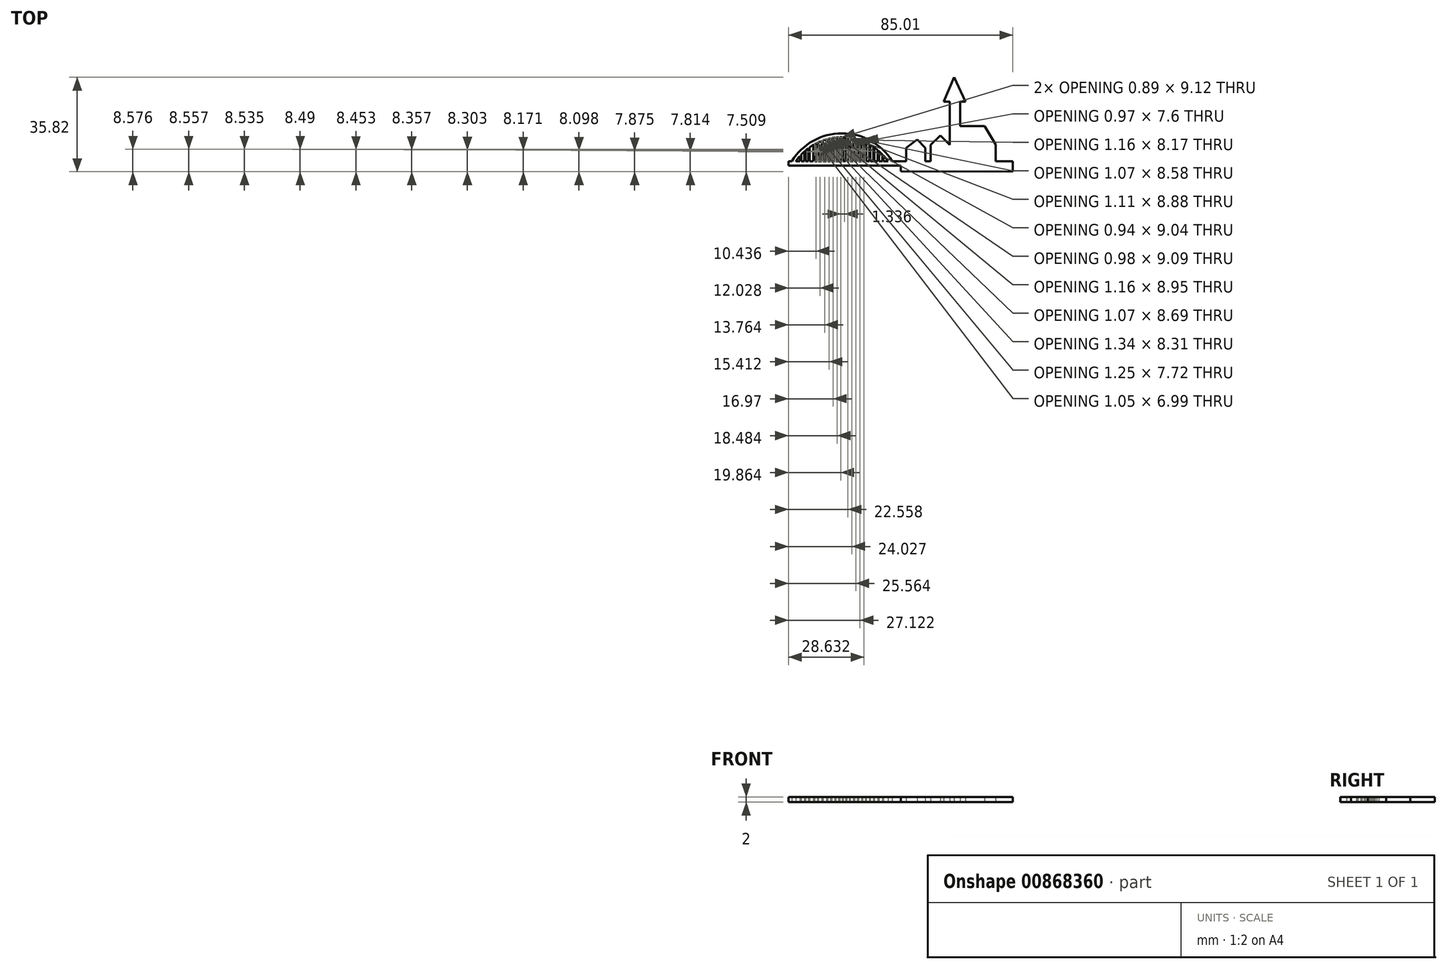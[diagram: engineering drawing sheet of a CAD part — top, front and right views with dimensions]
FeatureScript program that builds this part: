
annotation { "Feature Type Name" : "Feature", "Feature Type Description" : "" }
export const myFeature = defineFeature(function(context is Context, id is Id, definition is map)
    precondition{}
    {
        {
            var Q0;
            Q0=qCreatedBy(makeId("Top.planeOp"),FACE);
            var sketch = newSketch(context, id + "F0", { "sketchPlane" : qUnion([Q0])});
            skLineSegment(sketch, "E0.bottom", {"start": v(42.5, -30) * mm, "end": v(-42.5, -30) * mm});
            skLineSegment(sketch, "E0.top", {"start": v(42.5, 30) * mm, "end": v(-42.5, 30) * mm});
            skLineSegment(sketch, "E0.left", {"start": v(42.5, -30) * mm, "end": v(42.5, 30) * mm});
            skLineSegment(sketch, "E0.right", {"start": v(-42.5, -30) * mm, "end": v(-42.5, 30) * mm});
            skPoint(sketch, "E0.middle", {"position": v(0, 0) * mm});
            skSolve(sketch);
        }
        {
            var Q0;
            Q0=makeQuery(id+"F0.imprint","IMPRINT",FACE,{"disambiguationData":[TD([[makeQuery(id+"F0.imprint","IMPRINT",EDGE,{"derivedFrom":sQuery(id+"F0.wireOp",EDGE,"E0.bottom")}),-1.0]])]});
            var sketch = newSketch(context, id + "F1", { "sketchPlane" : qUnion([Q0])});
            skLineSegment(sketch, "E1.bottom", {"start": v(-42.57, -27.66) * mm, "end": v(0, -27.66) * mm});
            skLineSegment(sketch, "E1.top", {"start": v(-42.57, -25.97) * mm, "end": v(0, -25.97) * mm});
            skLineSegment(sketch, "E1.left", {"start": v(-42.57, -27.66) * mm, "end": v(-42.57, -25.97) * mm});
            skLineSegment(sketch, "E1.right", {"start": v(0, -27.66) * mm, "end": v(0, -25.97) * mm});
            skArc(sketch, "E2", {"start": v(-3.25, -25.97) * mm, "mid": v(-22.26, -15.39) * mm, "end": v(-41.27, -25.97) * mm});
            skArc(sketch, "E3", {"start": v(-4.87, -25.97) * mm, "mid": v(-22.33, -16.84) * mm, "end": v(-39.8, -25.97) * mm});
            skLineSegment(sketch, "E4", {"start": v(-33.34, -25.97) * mm, "end": v(-33.34, -19.92) * mm});
            skLineSegment(sketch, "E5", {"start": v(-33.34, -19.92) * mm, "end": v(-34.15, -20.43) * mm});
            skLineSegment(sketch, "E6", {"start": v(-34.15, -20.43) * mm, "end": v(-34.15, -25.97) * mm});
            skLineSegment(sketch, "E7", {"start": v(-34.15, -25.97) * mm, "end": v(-33.34, -25.97) * mm});
            skLineSegment(sketch, "E8", {"start": v(-36.62, -25.97) * mm, "end": v(-36.62, -22.36) * mm});
            skLineSegment(sketch, "E9", {"start": v(-36.62, -22.36) * mm, "end": v(-37.42, -23.12) * mm});
            skLineSegment(sketch, "E10", {"start": v(-37.42, -23.12) * mm, "end": v(-37.42, -25.97) * mm});
            skLineSegment(sketch, "E11", {"start": v(-37.42, -25.97) * mm, "end": v(-36.62, -25.97) * mm});
            skLineSegment(sketch, "E12", {"start": v(-30.9, -25.97) * mm, "end": v(-30.9, -18.65) * mm});
            skLineSegment(sketch, "E13", {"start": v(-30.9, -18.65) * mm, "end": v(-29.78, -18.2) * mm});
            skLineSegment(sketch, "E14", {"start": v(-29.78, -18.2) * mm, "end": v(-29.78, -25.97) * mm});
            skLineSegment(sketch, "E15", {"start": v(-29.78, -25.97) * mm, "end": v(-30.9, -25.97) * mm});
            skLineSegment(sketch, "E16", {"start": v(-27.67, -17.53) * mm, "end": v(-27.67, -25.97) * mm});
            skLineSegment(sketch, "E17", {"start": v(-27.67, -25.97) * mm, "end": v(-26.67, -25.97) * mm});
            skLineSegment(sketch, "E18", {"start": v(-26.67, -25.97) * mm, "end": v(-26.67, -17.3) * mm});
            skLineSegment(sketch, "E19", {"start": v(-26.67, -17.3) * mm, "end": v(-27.67, -17.53) * mm});
            skLineSegment(sketch, "E20", {"start": v(-24.95, -17) * mm, "end": v(-24.95, -25.97) * mm});
            skLineSegment(sketch, "E21", {"start": v(-24.95, -25.97) * mm, "end": v(-24.13, -25.97) * mm});
            skLineSegment(sketch, "E22", {"start": v(-24.13, -25.97) * mm, "end": v(-24.13, -16.92) * mm});
            skLineSegment(sketch, "E23", {"start": v(-24.13, -16.92) * mm, "end": v(-24.95, -17) * mm});
            skLineSegment(sketch, "E24", {"start": v(-22.33, -16.84) * mm, "end": v(-22.33, -25.97) * mm});
            skLineSegment(sketch, "E25", {"start": v(-22.33, -25.97) * mm, "end": v(-21.28, -25.97) * mm});
            skLineSegment(sketch, "E26", {"start": v(-21.28, -25.97) * mm, "end": v(-21.28, -16.87) * mm});
            skLineSegment(sketch, "E27", {"start": v(-21.28, -16.87) * mm, "end": v(-22.33, -16.84) * mm});
            skLineSegment(sketch, "E28", {"start": v(-19.68, -25.97) * mm, "end": v(-19.68, -17) * mm});
            skLineSegment(sketch, "E29", {"start": v(-19.68, -17) * mm, "end": v(-18.66, -17.16) * mm});
            skLineSegment(sketch, "E30", {"start": v(-18.66, -17.16) * mm, "end": v(-18.66, -25.97) * mm});
            skLineSegment(sketch, "E31", {"start": v(-18.66, -25.97) * mm, "end": v(-19.68, -25.97) * mm});
            skLineSegment(sketch, "E32", {"start": v(-17.03, -25.97) * mm, "end": v(-17.03, -17.51) * mm});
            skLineSegment(sketch, "E33", {"start": v(-17.03, -17.51) * mm, "end": v(-16, -17.8) * mm});
            skLineSegment(sketch, "E34", {"start": v(-16, -17.8) * mm, "end": v(-16, -25.97) * mm});
            skLineSegment(sketch, "E35", {"start": v(-16, -25.97) * mm, "end": v(-17.03, -25.97) * mm});
            skLineSegment(sketch, "E36", {"start": v(-14.54, -25.97) * mm, "end": v(-14.54, -18.32) * mm});
            skLineSegment(sketch, "E37", {"start": v(-14.54, -18.32) * mm, "end": v(-13.53, -18.75) * mm});
            skLineSegment(sketch, "E38", {"start": v(-13.53, -18.75) * mm, "end": v(-13.53, -25.97) * mm});
            skLineSegment(sketch, "E39", {"start": v(-13.53, -25.97) * mm, "end": v(-14.54, -25.97) * mm});
            skLineSegment(sketch, "E40", {"start": v(-11.58, -25.97) * mm, "end": v(-11.58, -19.76) * mm});
            skLineSegment(sketch, "E41", {"start": v(-11.58, -19.76) * mm, "end": v(-10.75, -20.27) * mm});
            skLineSegment(sketch, "E42", {"start": v(-10.75, -20.27) * mm, "end": v(-10.75, -25.97) * mm});
            skLineSegment(sketch, "E43", {"start": v(-10.75, -25.97) * mm, "end": v(-11.58, -25.97) * mm});
            skLineSegment(sketch, "E44", {"start": v(-9.2, -25.97) * mm, "end": v(-9.2, -21.38) * mm});
            skLineSegment(sketch, "E45", {"start": v(-9.2, -21.38) * mm, "end": v(-8.03, -22.36) * mm});
            skLineSegment(sketch, "E46", {"start": v(-8.03, -22.36) * mm, "end": v(-8.61, -21.87) * mm});
            skLineSegment(sketch, "E47", {"start": v(-8.61, -21.87) * mm, "end": v(-8.61, -25.97) * mm});
            skLineSegment(sketch, "E48", {"start": v(-8.61, -25.97) * mm, "end": v(-9.2, -25.97) * mm});
            skLineSegment(sketch, "E49", {"start": v(-7.28, -25.97) * mm, "end": v(-7.28, -23.07) * mm});
            skLineSegment(sketch, "E50", {"start": v(-7.28, -23.07) * mm, "end": v(-6.8, -23.57) * mm});
            skLineSegment(sketch, "E51", {"start": v(-6.8, -23.57) * mm, "end": v(-6.8, -25.97) * mm});
            skLineSegment(sketch, "E52", {"start": v(-6.8, -25.97) * mm, "end": v(-7.28, -25.97) * mm});
            skLineSegment(sketch, "E53", {"start": v(0, -29.8) * mm, "end": v(0, -25.97) * mm});
            skLineSegment(sketch, "E54", {"start": v(2.02, -25.97) * mm, "end": v(2.02, -20.96) * mm});
            skLineSegment(sketch, "E55", {"start": v(2.02, -20.96) * mm, "end": v(6.25, -17.79) * mm});
            skLineSegment(sketch, "E56", {"start": v(6.25, -17.79) * mm, "end": v(9.32, -20.96) * mm});
            skLineSegment(sketch, "E57", {"start": v(9.32, -20.96) * mm, "end": v(9.32, -25.97) * mm});
            skLineSegment(sketch, "E58", {"start": v(9.32, -25.97) * mm, "end": v(11.3, -25.97) * mm});
            skLineSegment(sketch, "E59", {"start": v(11.3, -25.97) * mm, "end": v(11.3, -19.72) * mm});
            skLineSegment(sketch, "E60", {"start": v(11.3, -19.72) * mm, "end": v(15, -16.15) * mm});
            skLineSegment(sketch, "E61", {"start": v(15, -16.15) * mm, "end": v(18.53, -19.8) * mm});
            skLineSegment(sketch, "E62", {"start": v(18.53, -19.8) * mm, "end": v(18.53, -25.97) * mm});
            skLineSegment(sketch, "E63", {"start": v(18.53, -25.97) * mm, "end": v(18.53, -3.42) * mm});
            skLineSegment(sketch, "E64", {"start": v(18.53, -3.42) * mm, "end": v(16.26, -3.42) * mm});
            skLineSegment(sketch, "E65", {"start": v(16.26, -3.42) * mm, "end": v(20.2, 5.84) * mm});
            skLineSegment(sketch, "E66", {"start": v(20.2, 5.84) * mm, "end": v(24.53, -3.42) * mm});
            skLineSegment(sketch, "E67", {"start": v(24.53, -3.42) * mm, "end": v(22.49, -3.42) * mm});
            skLineSegment(sketch, "E68", {"start": v(22.49, -3.42) * mm, "end": v(22.49, -19.63) * mm});
            skLineSegment(sketch, "E69", {"start": v(22.49, -19.63) * mm, "end": v(22.49, -12.61) * mm});
            skLineSegment(sketch, "E70", {"start": v(22.49, -12.61) * mm, "end": v(31.8, -12.61) * mm});
            skLineSegment(sketch, "E71", {"start": v(31.8, -12.61) * mm, "end": v(35.96, -19.63) * mm});
            skLineSegment(sketch, "E72", {"start": v(35.96, -19.63) * mm, "end": v(35.96, -25.97) * mm});
            skLineSegment(sketch, "E73", {"start": v(35.96, -25.97) * mm, "end": v(37.84, -25.97) * mm});
            skLineSegment(sketch, "E74", {"start": v(37.84, -25.97) * mm, "end": v(42.44, -25.97) * mm});
            skLineSegment(sketch, "E75", {"start": v(42.44, -25.97) * mm, "end": v(42.44, -29.98) * mm});
            skLineSegment(sketch, "E76", {"start": v(42.44, -29.98) * mm, "end": v(0, -29.8) * mm});
            skLineSegment(sketch, "E77", {"start": v(0, -25.97) * mm, "end": v(2.02, -25.97) * mm});
            skSolve(sketch);
        }
        {
            var Q0;
            Q0 = qSketchRegion(id + "F1", true);
            extrude(context, id + "F2", {"entities" : qUnion([Q0]), "depth" : 2 * mm, "offsetDistance" : 25 * mm});
        }
        {
            var Q0;
            Q0=makeQuery(id+"F0.imprint","IMPRINT",FACE,{"disambiguationData":[TD([[makeQuery(id+"F0.imprint","IMPRINT",EDGE,{"derivedFrom":sQuery(id+"F0.wireOp",EDGE,"E0.bottom")}),-1.0]])]});
            var sketch = newSketch(context, id + "F3", { "sketchPlane" : qUnion([Q0])});
            skLineSegment(sketch, "E78.bottom", {"start": v(-38.16, -26.15) * mm, "end": v(-37.76, -26.15) * mm});
            skLineSegment(sketch, "E78.top", {"start": v(-38.16, -23.06) * mm, "end": v(-37.76, -23.06) * mm});
            skLineSegment(sketch, "E78.left", {"start": v(-38.16, -26.15) * mm, "end": v(-38.16, -23.06) * mm});
            skLineSegment(sketch, "E78.right", {"start": v(-37.76, -26.15) * mm, "end": v(-37.76, -23.06) * mm});
            skLineSegment(sketch, "E79.bottom", {"start": v(-36.55, -26.06) * mm, "end": v(-36.1, -26.06) * mm});
            skLineSegment(sketch, "E79.top", {"start": v(-36.55, -21.75) * mm, "end": v(-36.1, -21.75) * mm});
            skLineSegment(sketch, "E79.left", {"start": v(-36.55, -26.06) * mm, "end": v(-36.55, -21.75) * mm});
            skLineSegment(sketch, "E79.right", {"start": v(-36.1, -26.06) * mm, "end": v(-36.1, -21.75) * mm});
            skLineSegment(sketch, "E80.bottom", {"start": v(-35, -26.02) * mm, "end": v(-34.55, -26.02) * mm});
            skLineSegment(sketch, "E80.top", {"start": v(-35, -20.45) * mm, "end": v(-34.55, -20.45) * mm});
            skLineSegment(sketch, "E80.left", {"start": v(-35, -26.02) * mm, "end": v(-35, -20.45) * mm});
            skLineSegment(sketch, "E80.right", {"start": v(-34.55, -26.02) * mm, "end": v(-34.55, -20.45) * mm});
            skLineSegment(sketch, "E81.bottom", {"start": v(-33.1, -26.02) * mm, "end": v(-32.66, -26.02) * mm});
            skLineSegment(sketch, "E81.top", {"start": v(-33.1, -19.3) * mm, "end": v(-32.66, -19.3) * mm});
            skLineSegment(sketch, "E81.left", {"start": v(-33.1, -26.02) * mm, "end": v(-33.1, -19.3) * mm});
            skLineSegment(sketch, "E81.right", {"start": v(-32.66, -26.02) * mm, "end": v(-32.66, -19.3) * mm});
            skLineSegment(sketch, "E82.bottom", {"start": v(-31.61, -26.06) * mm, "end": v(-31.17, -26.06) * mm});
            skLineSegment(sketch, "E82.top", {"start": v(-31.61, -18.34) * mm, "end": v(-31.17, -18.34) * mm});
            skLineSegment(sketch, "E82.left", {"start": v(-31.61, -26.06) * mm, "end": v(-31.61, -18.34) * mm});
            skLineSegment(sketch, "E82.right", {"start": v(-31.17, -26.06) * mm, "end": v(-31.17, -18.34) * mm});
            skLineSegment(sketch, "E83.bottom", {"start": v(-29.92, -26.06) * mm, "end": v(-29.47, -26.06) * mm});
            skLineSegment(sketch, "E83.top", {"start": v(-29.92, -17.7) * mm, "end": v(-29.47, -17.7) * mm});
            skLineSegment(sketch, "E83.left", {"start": v(-29.92, -26.06) * mm, "end": v(-29.92, -17.7) * mm});
            skLineSegment(sketch, "E83.right", {"start": v(-29.47, -26.06) * mm, "end": v(-29.47, -17.7) * mm});
            skLineSegment(sketch, "E84.bottom", {"start": v(-28.14, -26.1) * mm, "end": v(-27.7, -26.1) * mm});
            skLineSegment(sketch, "E84.top", {"start": v(-28.14, -17.27) * mm, "end": v(-27.7, -17.27) * mm});
            skLineSegment(sketch, "E84.left", {"start": v(-28.14, -26.1) * mm, "end": v(-28.14, -17.27) * mm});
            skLineSegment(sketch, "E84.right", {"start": v(-27.7, -26.1) * mm, "end": v(-27.7, -17.27) * mm});
            skLineSegment(sketch, "E85.bottom", {"start": v(-26.62, -26.09) * mm, "end": v(-26.18, -26.09) * mm});
            skLineSegment(sketch, "E85.top", {"start": v(-26.62, -16.98) * mm, "end": v(-26.18, -16.98) * mm});
            skLineSegment(sketch, "E85.left", {"start": v(-26.62, -26.09) * mm, "end": v(-26.62, -16.98) * mm});
            skLineSegment(sketch, "E85.right", {"start": v(-26.18, -26.09) * mm, "end": v(-26.18, -16.98) * mm});
            skLineSegment(sketch, "E86.bottom", {"start": v(-25.02, -26.09) * mm, "end": v(-24.58, -26.09) * mm});
            skLineSegment(sketch, "E86.top", {"start": v(-25.02, -16.58) * mm, "end": v(-24.58, -16.58) * mm});
            skLineSegment(sketch, "E86.left", {"start": v(-25.02, -26.09) * mm, "end": v(-25.02, -16.58) * mm});
            skLineSegment(sketch, "E86.right", {"start": v(-24.58, -26.09) * mm, "end": v(-24.58, -16.58) * mm});
            skLineSegment(sketch, "E87.bottom", {"start": v(-23.6, -26.09) * mm, "end": v(-23.15, -26.09) * mm});
            skLineSegment(sketch, "E87.top", {"start": v(-23.6, -16.58) * mm, "end": v(-23.15, -16.58) * mm});
            skLineSegment(sketch, "E87.left", {"start": v(-23.6, -26.09) * mm, "end": v(-23.6, -16.58) * mm});
            skLineSegment(sketch, "E87.right", {"start": v(-23.15, -26.09) * mm, "end": v(-23.15, -16.58) * mm});
            skLineSegment(sketch, "E88.bottom", {"start": v(-22.26, -26.02) * mm, "end": v(-21.82, -26.02) * mm});
            skLineSegment(sketch, "E88.top", {"start": v(-22.26, -16.58) * mm, "end": v(-21.82, -16.58) * mm});
            skLineSegment(sketch, "E88.left", {"start": v(-22.26, -26.02) * mm, "end": v(-22.26, -16.58) * mm});
            skLineSegment(sketch, "E88.right", {"start": v(-21.82, -26.02) * mm, "end": v(-21.82, -16.58) * mm});
            skLineSegment(sketch, "E89.bottom", {"start": v(-20.92, -26.09) * mm, "end": v(-20.48, -26.09) * mm});
            skLineSegment(sketch, "E89.top", {"start": v(-20.92, -16.58) * mm, "end": v(-20.48, -16.58) * mm});
            skLineSegment(sketch, "E89.left", {"start": v(-20.92, -26.09) * mm, "end": v(-20.92, -16.58) * mm});
            skLineSegment(sketch, "E89.right", {"start": v(-20.48, -26.09) * mm, "end": v(-20.48, -16.58) * mm});
            skLineSegment(sketch, "E90.bottom", {"start": v(-19.54, -26.02) * mm, "end": v(-19.1, -26.02) * mm});
            skLineSegment(sketch, "E90.top", {"start": v(-19.54, -16.58) * mm, "end": v(-19.1, -16.58) * mm});
            skLineSegment(sketch, "E90.left", {"start": v(-19.54, -26.02) * mm, "end": v(-19.54, -16.58) * mm});
            skLineSegment(sketch, "E90.right", {"start": v(-19.1, -26.02) * mm, "end": v(-19.1, -16.58) * mm});
            skLineSegment(sketch, "E91.bottom", {"start": v(-17.99, -26.02) * mm, "end": v(-17.54, -26.02) * mm});
            skLineSegment(sketch, "E91.top", {"start": v(-17.99, -16.58) * mm, "end": v(-17.54, -16.58) * mm});
            skLineSegment(sketch, "E91.left", {"start": v(-17.99, -26.02) * mm, "end": v(-17.99, -16.58) * mm});
            skLineSegment(sketch, "E91.right", {"start": v(-17.54, -26.02) * mm, "end": v(-17.54, -16.58) * mm});
            skLineSegment(sketch, "E92.bottom", {"start": v(-16.03, -26.1) * mm, "end": v(-16.47, -26.1) * mm});
            skLineSegment(sketch, "E92.top", {"start": v(-16.03, -17.03) * mm, "end": v(-16.47, -17.03) * mm});
            skLineSegment(sketch, "E92.left", {"start": v(-16.03, -26.1) * mm, "end": v(-16.03, -17.03) * mm});
            skLineSegment(sketch, "E92.right", {"start": v(-16.47, -26.1) * mm, "end": v(-16.47, -17.03) * mm});
            skLineSegment(sketch, "E93.bottom", {"start": v(-14.87, -26.06) * mm, "end": v(-14.42, -26.06) * mm});
            skLineSegment(sketch, "E93.top", {"start": v(-14.87, -17.6) * mm, "end": v(-14.42, -17.6) * mm});
            skLineSegment(sketch, "E93.left", {"start": v(-14.87, -26.06) * mm, "end": v(-14.87, -17.6) * mm});
            skLineSegment(sketch, "E93.right", {"start": v(-14.42, -26.06) * mm, "end": v(-14.42, -17.6) * mm});
            skLineSegment(sketch, "E94.bottom", {"start": v(-13.45, -26.04) * mm, "end": v(-13, -26.04) * mm});
            skLineSegment(sketch, "E94.top", {"start": v(-13.45, -17.87) * mm, "end": v(-13, -17.87) * mm});
            skLineSegment(sketch, "E94.left", {"start": v(-13.45, -26.04) * mm, "end": v(-13.45, -17.87) * mm});
            skLineSegment(sketch, "E94.right", {"start": v(-13, -26.04) * mm, "end": v(-13, -17.87) * mm});
            skLineSegment(sketch, "E95.bottom", {"start": v(-11.95, -26.04) * mm, "end": v(-11.5, -26.04) * mm});
            skLineSegment(sketch, "E95.top", {"start": v(-11.95, -19.27) * mm, "end": v(-11.5, -19.27) * mm});
            skLineSegment(sketch, "E95.left", {"start": v(-11.95, -26.04) * mm, "end": v(-11.95, -19.27) * mm});
            skLineSegment(sketch, "E95.right", {"start": v(-11.5, -26.04) * mm, "end": v(-11.5, -19.27) * mm});
            skLineSegment(sketch, "E96.bottom", {"start": v(-10.44, -26.11) * mm, "end": v(-10, -26.11) * mm});
            skLineSegment(sketch, "E96.top", {"start": v(-10.44, -20.38) * mm, "end": v(-10, -20.38) * mm});
            skLineSegment(sketch, "E96.left", {"start": v(-10.44, -26.11) * mm, "end": v(-10.44, -20.38) * mm});
            skLineSegment(sketch, "E96.right", {"start": v(-10, -26.11) * mm, "end": v(-10, -20.38) * mm});
            skLineSegment(sketch, "E97.bottom", {"start": v(-8.7, -26.06) * mm, "end": v(-8.25, -26.06) * mm});
            skLineSegment(sketch, "E97.top", {"start": v(-8.7, -21.38) * mm, "end": v(-8.25, -21.38) * mm});
            skLineSegment(sketch, "E97.left", {"start": v(-8.7, -26.06) * mm, "end": v(-8.7, -21.38) * mm});
            skLineSegment(sketch, "E97.right", {"start": v(-8.25, -26.06) * mm, "end": v(-8.25, -21.38) * mm});
            skLineSegment(sketch, "E98.bottom", {"start": v(-7.03, -26.1) * mm, "end": v(-6.57, -26.1) * mm});
            skLineSegment(sketch, "E98.top", {"start": v(-7.03, -22.55) * mm, "end": v(-6.57, -22.55) * mm});
            skLineSegment(sketch, "E98.left", {"start": v(-7.03, -26.1) * mm, "end": v(-7.03, -22.55) * mm});
            skLineSegment(sketch, "E98.right", {"start": v(-6.57, -26.1) * mm, "end": v(-6.57, -22.55) * mm});
            skSolve(sketch);
        }
        {
            var Q0;
            Q0 = qSketchRegion(id + "F3", true);
            extrude(context, id + "F4", {"entities" : qUnion([Q0]), "operationType" : NewBodyOperationType.ADD, "depth" : 2 * mm, "offsetDistance" : 25 * mm});
        }
    });
